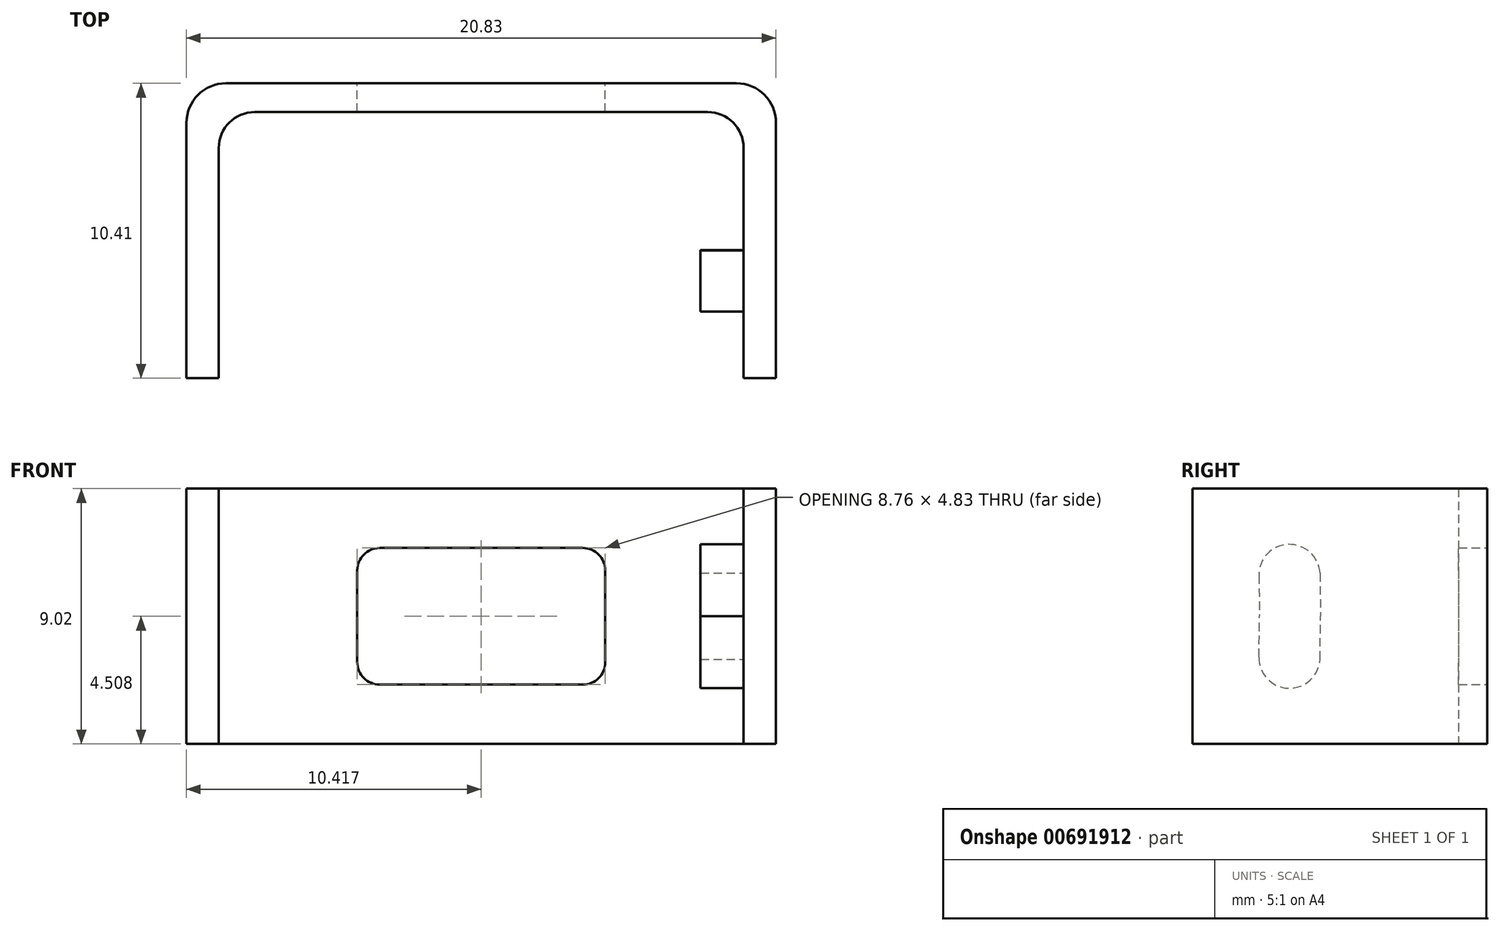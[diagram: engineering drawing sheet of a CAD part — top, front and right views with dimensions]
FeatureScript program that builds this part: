
annotation { "Feature Type Name" : "Feature", "Feature Type Description" : "" }
export const myFeature = defineFeature(function(context is Context, id is Id, definition is map)
    precondition{}
    {
        {
            var Q0;
            Q0=qCreatedBy(makeId("Top.planeOp"),FACE);
            var sketch = newSketch(context, id + "F0", { "sketchPlane" : qUnion([Q0])});
            skLineSegment(sketch, "E0", {"start": v(0, 0) * mm, "end": v(0, 9.02) * mm});
            skLineSegment(sketch, "E1", {"start": v(1.27, 10.29) * mm, "end": v(19.3, 10.29) * mm});
            skLineSegment(sketch, "E2", {"start": v(20.57, 9.02) * mm, "end": v(20.57, 0) * mm});
            skLineSegment(sketch, "E3", {"start": v(20.57, 0) * mm, "end": v(19.56, 0) * mm});
            skLineSegment(sketch, "E4", {"start": v(19.56, 0) * mm, "end": v(19.56, 8.13) * mm});
            skLineSegment(sketch, "E5", {"start": v(18.29, 9.4) * mm, "end": v(2.29, 9.4) * mm});
            skLineSegment(sketch, "E6", {"start": v(1.02, 8.13) * mm, "end": v(1.02, 0) * mm});
            skLineSegment(sketch, "E7", {"start": v(1.02, 0) * mm, "end": v(0, 0) * mm});
            skPoint(sketch, "E8.visualSharp", {"position": v(1.02, 9.4) * mm});
            skArc(sketch, "E8.filletArc", {"start": v(2.29, 9.4) * mm, "mid": v(1.39, 9.03) * mm, "end": v(1.02, 8.13) * mm});
            skPoint(sketch, "E9.visualSharp", {"position": v(0, 10.29) * mm});
            skArc(sketch, "E9.filletArc", {"start": v(1.27, 10.29) * mm, "mid": v(0.37, 9.92) * mm, "end": v(0, 9.02) * mm});
            skPoint(sketch, "E10.visualSharp", {"position": v(20.57, 10.29) * mm});
            skArc(sketch, "E10.filletArc", {"start": v(20.57, 9.02) * mm, "mid": v(20.2, 9.92) * mm, "end": v(19.3, 10.29) * mm});
            skPoint(sketch, "E11.visualSharp", {"position": v(19.56, 9.4) * mm});
            skArc(sketch, "E11.filletArc", {"start": v(19.56, 8.13) * mm, "mid": v(19.19, 9.03) * mm, "end": v(18.29, 9.4) * mm});
            skSolve(sketch);
        }
        {
            var Q0;
            Q0 = qSketchRegion(id + "F0", true);
            extrude(context, id + "F1", {"entities" : qUnion([Q0]), "depth" : 9.02 * mm, "offsetDistance" : 25.4 * mm});
        }
        {
            var Q0;
            Q0=makeQuery(id+"F1.opExtrude","SWEPT_FACE",FACE,{"disambiguationData":[OSD([sQuery(id+"F0.wireOp",EDGE,"E1")])]});
            var sketch = newSketch(context, id + "F2", { "sketchPlane" : qUnion([Q0])});
            skLineSegment(sketch, "E12", {"start": v(-10.29, 0) * mm, "end": v(-10.29, 9.02) * mm, "construction": true});
            skLineSegment(sketch, "E13", {"start": v(-1.27, 4.5) * mm, "end": v(-19.3, 4.5) * mm, "construction": true});
            skLineSegment(sketch, "E14.bottom", {"start": v(-6.7, 2.1) * mm, "end": v(-13.87, 2.1) * mm});
            skLineSegment(sketch, "E14.top", {"start": v(-6.7, 6.92) * mm, "end": v(-13.87, 6.92) * mm});
            skLineSegment(sketch, "E14.left", {"start": v(-5.9, 2.89) * mm, "end": v(-5.9, 6.13) * mm});
            skLineSegment(sketch, "E14.right", {"start": v(-14.67, 2.89) * mm, "end": v(-14.67, 6.13) * mm});
            skPoint(sketch, "E14.middle", {"position": v(-10.29, 4.5) * mm});
            skPoint(sketch, "E15.visualSharp", {"position": v(-5.9, 2.1) * mm});
            skArc(sketch, "E15.filletArc", {"start": v(-6.7, 2.1) * mm, "mid": v(-6.14, 2.33) * mm, "end": v(-5.9, 2.89) * mm});
            skPoint(sketch, "E16.visualSharp", {"position": v(-14.67, 2.1) * mm});
            skArc(sketch, "E16.filletArc", {"start": v(-14.67, 2.89) * mm, "mid": v(-14.44, 2.33) * mm, "end": v(-13.87, 2.1) * mm});
            skPoint(sketch, "E17.visualSharp", {"position": v(-14.67, 6.92) * mm});
            skArc(sketch, "E17.filletArc", {"start": v(-13.87, 6.92) * mm, "mid": v(-14.44, 6.69) * mm, "end": v(-14.67, 6.13) * mm});
            skPoint(sketch, "E18.visualSharp", {"position": v(-5.9, 6.92) * mm});
            skArc(sketch, "E18.filletArc", {"start": v(-5.9, 6.13) * mm, "mid": v(-6.14, 6.69) * mm, "end": v(-6.7, 6.92) * mm});
            skSolve(sketch);
        }
        {
            var Q0;
            Q0 = qSketchRegion(id + "F2", true);
            extrude(context, id + "F3", {"entities" : qUnion([Q0]), "operationType" : NewBodyOperationType.REMOVE, "endBound" : BoundingType.THROUGH_ALL, "oppositeDirection" : true, "depth" : 25.4 * mm, "offsetDistance" : 25.4 * mm});
        }
        {
            var Q0;
            Q0=makeQuery(id+"F1.opExtrude","SWEPT_FACE",FACE,{"disambiguationData":[OSD([sQuery(id+"F0.wireOp",EDGE,"E2")])]});
            var sketch = newSketch(context, id + "F4", { "sketchPlane" : qUnion([Q0])});
            skLineSegment(sketch, "E19", {"start": v(9.02, 4.5) * mm, "end": v(0, 4.5) * mm, "construction": true});
            skLineSegment(sketch, "E20.left", {"start": v(4.53, 4.5) * mm, "end": v(4.5, 2.98) * mm});
            skLineSegment(sketch, "E20.right", {"start": v(2.37, 4.5) * mm, "end": v(2.35, 3.06) * mm});
            skArc(sketch, "E21", {"start": v(2.35, 3.06) * mm, "mid": v(3.39, 1.97) * mm, "end": v(4.5, 2.98) * mm});
            skLineSegment(sketch, "E22.MirrorCS", {"start": v(4.53, 4.5) * mm, "end": v(4.5, 6.03) * mm});
            skLineSegment(sketch, "E23.MirrorCS", {"start": v(2.37, 4.5) * mm, "end": v(2.35, 5.95) * mm});
            skArc(sketch, "E24.MirrorCS", {"start": v(2.35, 5.95) * mm, "mid": v(3.39, 7.05) * mm, "end": v(4.5, 6.03) * mm});
            skSolve(sketch);
        }
        {
            var Q0;
            Q0 = qSketchRegion(id + "F4", true);
            extrude(context, id + "F5", {"entities" : qUnion([Q0]), "operationType" : NewBodyOperationType.ADD, "oppositeDirection" : true, "depth" : 2.54 * mm, "offsetDistance" : 25.4 * mm});
        }
        {
            var Q0;
            Q0=makeQuery(id+"F1.opExtrude","CAP_FACE",FACE,{"disambiguationData":[OSD([sQuery(id+"F0.wireOp",EDGE,"E0"),sQuery(id+"F0.wireOp",EDGE,"E1"),sQuery(id+"F0.wireOp",EDGE,"E2"),sQuery(id+"F0.wireOp",EDGE,"E3"),sQuery(id+"F0.wireOp",EDGE,"E4"),sQuery(id+"F0.wireOp",EDGE,"E5"),sQuery(id+"F0.wireOp",EDGE,"E6"),sQuery(id+"F0.wireOp",EDGE,"E7"),sQuery(id+"F0.wireOp",EDGE,"E8.filletArc"),sQuery(id+"F0.wireOp",EDGE,"E9.filletArc"),sQuery(id+"F0.wireOp",EDGE,"E10.filletArc"),sQuery(id+"F0.wireOp",EDGE,"E11.filletArc")])],"isStart":true});
            var sketch = newSketch(context, id + "F6", { "sketchPlane" : qUnion([Q0])});
            skLineSegment(sketch, "E25.0", {"start": v(20.57, -9.02) * mm, "end": v(20.57, 0) * mm});
            skArc(sketch, "E26.0", {"start": v(20.57, -9.02) * mm, "mid": v(20.2, -9.92) * mm, "end": v(19.3, -10.29) * mm});
            skLineSegment(sketch, "E27.0", {"start": v(1.27, -10.29) * mm, "end": v(19.3, -10.29) * mm});
            skArc(sketch, "E28.0", {"start": v(1.27, -10.29) * mm, "mid": v(0.37, -9.92) * mm, "end": v(0, -9.02) * mm});
            skLineSegment(sketch, "E29.0", {"start": v(0, 0) * mm, "end": v(0, -9.02) * mm});
            skLineSegment(sketch, "E30.0", {"start": v(-0.13, 0) * mm, "end": v(-0.13, -9.02) * mm});
            skLineSegment(sketch, "E30.1", {"start": v(20.7, -9.02) * mm, "end": v(20.7, 0) * mm});
            skArc(sketch, "E30.2", {"start": v(20.7, -9.02) * mm, "mid": v(20.3, -10) * mm, "end": v(19.3, -10.41) * mm});
            skLineSegment(sketch, "E30.3", {"start": v(1.27, -10.41) * mm, "end": v(19.3, -10.41) * mm});
            skArc(sketch, "E30.4", {"start": v(1.27, -10.41) * mm, "mid": v(0.28, -10) * mm, "end": v(-0.13, -9.02) * mm});
            skLineSegment(sketch, "E31", {"start": v(20.57, 0) * mm, "end": v(20.7, 0) * mm});
            skLineSegment(sketch, "E32", {"start": v(0, 0) * mm, "end": v(-0.13, 0) * mm});
            skSolve(sketch);
        }
        {
            var Q0;
            Q0 = qSketchRegion(id + "F6", true);
            var Q1;
            Q1=makeQuery(id+"F1.opExtrude","CAP_FACE",FACE,{"disambiguationData":[OSD([sQuery(id+"F0.wireOp",EDGE,"E0"),sQuery(id+"F0.wireOp",EDGE,"E1"),sQuery(id+"F0.wireOp",EDGE,"E2"),sQuery(id+"F0.wireOp",EDGE,"E3"),sQuery(id+"F0.wireOp",EDGE,"E4"),sQuery(id+"F0.wireOp",EDGE,"E5"),sQuery(id+"F0.wireOp",EDGE,"E6"),sQuery(id+"F0.wireOp",EDGE,"E7"),sQuery(id+"F0.wireOp",EDGE,"E8.filletArc"),sQuery(id+"F0.wireOp",EDGE,"E9.filletArc"),sQuery(id+"F0.wireOp",EDGE,"E10.filletArc"),sQuery(id+"F0.wireOp",EDGE,"E11.filletArc")])],"isStart":false});
            var Q2;
            Q2=makeQuery(id+"F1.opExtrude","SWEPT_BODY",BODY,{"disambiguationData":[OSD([sQuery(id+"F0.wireOp",EDGE,"E0"),sQuery(id+"F0.wireOp",EDGE,"E1"),sQuery(id+"F0.wireOp",EDGE,"E2"),sQuery(id+"F0.wireOp",EDGE,"E3"),sQuery(id+"F0.wireOp",EDGE,"E4"),sQuery(id+"F0.wireOp",EDGE,"E5"),sQuery(id+"F0.wireOp",EDGE,"E6"),sQuery(id+"F0.wireOp",EDGE,"E7"),sQuery(id+"F0.wireOp",EDGE,"E8.filletArc"),sQuery(id+"F0.wireOp",EDGE,"E9.filletArc"),sQuery(id+"F0.wireOp",EDGE,"E10.filletArc"),sQuery(id+"F0.wireOp",EDGE,"E11.filletArc")])]});
            extrude(context, id + "F7", {"entities" : qUnion([Q0]), "operationType" : NewBodyOperationType.ADD, "endBound" : BoundingType.UP_TO_SURFACE, "oppositeDirection" : true, "depth" : 25.4 * mm, "endBoundEntityFace" : qUnion([Q1]), "endBoundEntityBody" : qUnion([Q2]), "offsetDistance" : 25.4 * mm});
        }
        {
            var Q0;
            Q0=makeQuery(id+"F7.opExtrude","SWEPT_FACE",FACE,{"disambiguationData":[OSD([sQuery(id+"F6.wireOp",EDGE,"E27.0")])]});
            var sketch = newSketch(context, id + "F8", { "sketchPlane" : qUnion([Q0])});
            skLineSegment(sketch, "E33.0", {"start": v(6.7, 2.1) * mm, "end": v(13.87, 2.1) * mm});
            skArc(sketch, "E33.1", {"start": v(14.67, 2.89) * mm, "mid": v(14.44, 2.33) * mm, "end": v(13.87, 2.1) * mm});
            skLineSegment(sketch, "E33.2", {"start": v(14.67, 2.89) * mm, "end": v(14.67, 6.13) * mm});
            skArc(sketch, "E33.3", {"start": v(6.7, 2.1) * mm, "mid": v(6.14, 2.33) * mm, "end": v(5.9, 2.89) * mm});
            skLineSegment(sketch, "E33.4", {"start": v(5.9, 2.89) * mm, "end": v(5.9, 6.13) * mm});
            skArc(sketch, "E33.5", {"start": v(5.9, 6.13) * mm, "mid": v(6.14, 6.69) * mm, "end": v(6.7, 6.92) * mm});
            skLineSegment(sketch, "E33.6", {"start": v(6.7, 6.92) * mm, "end": v(13.87, 6.92) * mm});
            skArc(sketch, "E33.7", {"start": v(13.87, 6.92) * mm, "mid": v(14.44, 6.69) * mm, "end": v(14.67, 6.13) * mm});
            skSolve(sketch);
        }
        {
            var Q0;
            Q0 = qSketchRegion(id + "F8", true);
            extrude(context, id + "F9", {"entities" : qUnion([Q0]), "operationType" : NewBodyOperationType.REMOVE, "oppositeDirection" : true, "depth" : 25.4 * mm, "offsetDistance" : 25.4 * mm});
        }
    });
